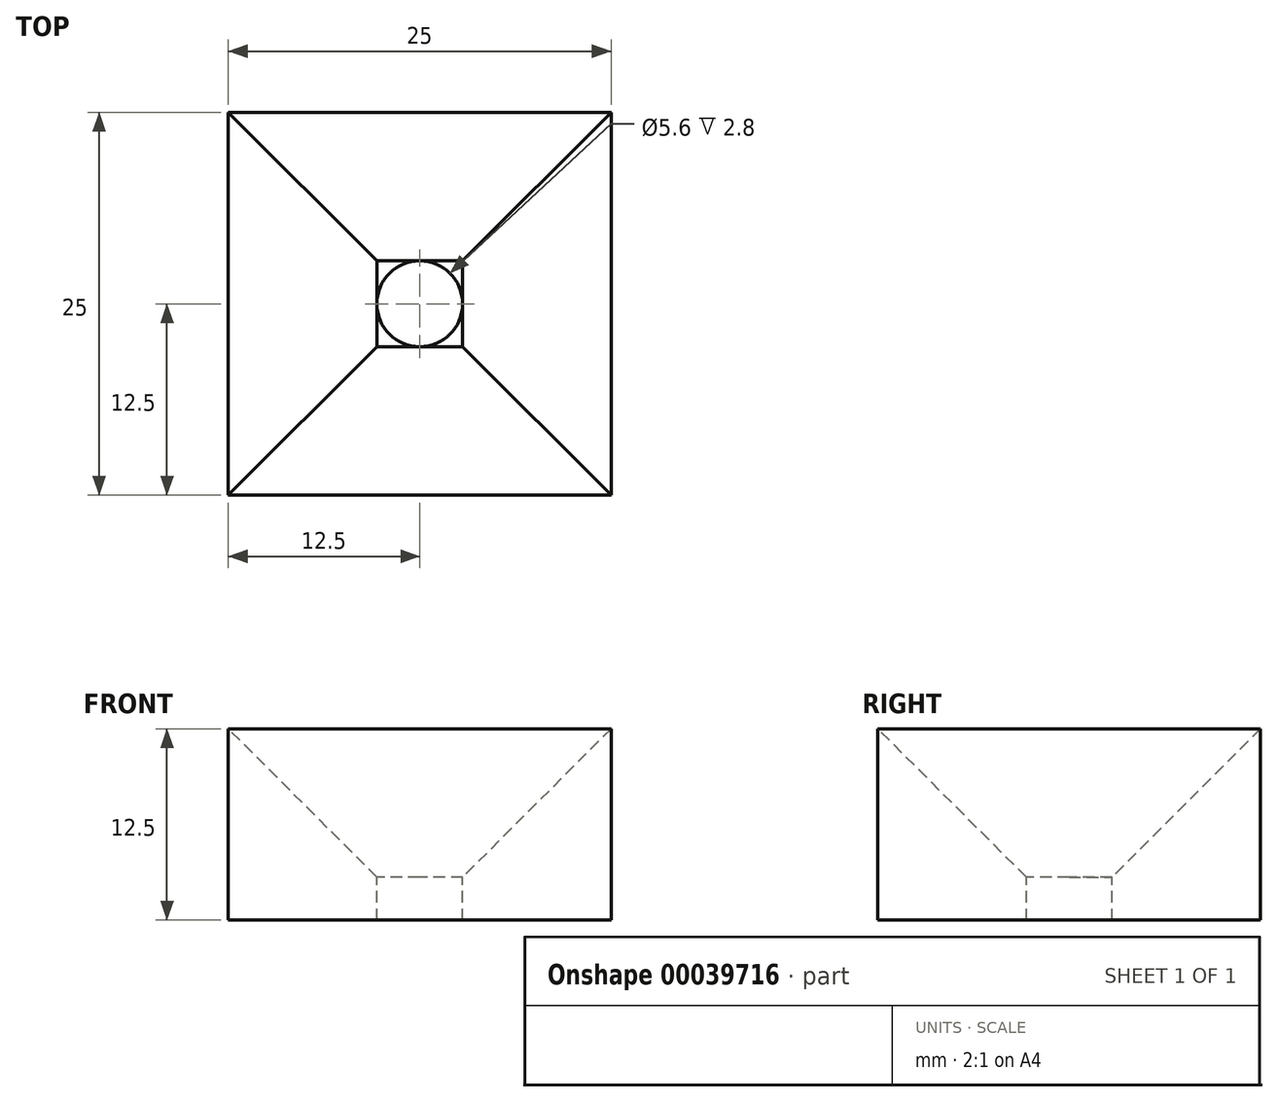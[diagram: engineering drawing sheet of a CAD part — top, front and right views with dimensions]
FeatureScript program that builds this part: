
annotation { "Feature Type Name" : "Feature", "Feature Type Description" : "" }
export const myFeature = defineFeature(function(context is Context, id is Id, definition is map)
    precondition{}
    {
        {
            var Q0;
            Q0=qCreatedBy(makeId("Front.planeOp"),FACE);
            var sketch = newSketch(context, id + "F0", { "sketchPlane" : qUnion([Q0])});
            skLineSegment(sketch, "E0.bottom", {"start": v(-12.5, 0) * mm, "end": v(12.5, 0) * mm});
            skLineSegment(sketch, "E0.top", {"start": v(-12.5, 12.5) * mm, "end": v(12.5, 12.5) * mm, "construction": true});
            skLineSegment(sketch, "E0.left", {"start": v(-12.5, 0) * mm, "end": v(-12.5, 12.5) * mm});
            skLineSegment(sketch, "E0.right", {"start": v(12.5, 0) * mm, "end": v(12.5, 12.5) * mm});
            skLineSegment(sketch, "E1", {"start": v(-12.5, 12.5) * mm, "end": v(0, 0) * mm});
            skLineSegment(sketch, "E2", {"start": v(0, 0) * mm, "end": v(12.5, 12.5) * mm});
            skLineSegment(sketch, "E3", {"start": v(-2.8, 2.8) * mm, "end": v(2.8, 2.8) * mm});
            skSolve(sketch);
        }
        {
            var Q0;
            Q0 = qSketchRegion(id + "F0", true);
            extrude(context, id + "F1", {"entities" : qUnion([Q0]), "oppositeDirection" : true, "depth" : 25 * mm});
        }
        {
            var Q0;
            Q0=makeQuery(id+"F1.opExtrude","SWEPT_FACE",FACE,{"disambiguationData":[OSD([sQuery(id+"F0.wireOp",EDGE,"E0.right")])]});
            var sketch = newSketch(context, id + "F2", { "sketchPlane" : qUnion([Q0])});
            skLineSegment(sketch, "E4", {"start": v(12.5, 0) * mm, "end": v(0, 12.5) * mm});
            skLineSegment(sketch, "E5", {"start": v(0, 12.5) * mm, "end": v(0, 0) * mm});
            skLineSegment(sketch, "E6", {"start": v(0, 0) * mm, "end": v(12.5, 0) * mm});
            skLineSegment(sketch, "E7", {"start": v(25, 12.5) * mm, "end": v(12.5, 0) * mm});
            skLineSegment(sketch, "E8", {"start": v(25, 0) * mm, "end": v(25, 12.5) * mm});
            skLineSegment(sketch, "E9", {"start": v(12.5, 0) * mm, "end": v(25, 0) * mm});
            skSolve(sketch);
        }
        {
            var Q0;
            Q0 = qSketchRegion(id + "F2", true);
            extrude(context, id + "F3", {"entities" : qUnion([Q0]), "operationType" : NewBodyOperationType.ADD, "oppositeDirection" : true, "depth" : 25 * mm});
        }
        {
            var Q0;
            Q0=makeQuery(id+"F1.opExtrude","SWEPT_FACE",FACE,{"disambiguationData":[OSD([sQuery(id+"F0.wireOp",EDGE,"E3")])]});
            var sketch = newSketch(context, id + "F4", { "sketchPlane" : qUnion([Q0])});
            skCircle(sketch, "E10", {"center": v(0, 12.5) * mm, "radius": 2.8 * mm});
            skPoint(sketch, "E10.centerSnap0", {"position": v(-2.8, 12.5) * mm});
            skSolve(sketch);
        }
        {
            var Q0;
            Q0 = qSketchRegion(id + "F4", true);
            extrude(context, id + "F5", {"entities" : qUnion([Q0]), "operationType" : NewBodyOperationType.REMOVE, "endBound" : BoundingType.THROUGH_ALL, "oppositeDirection" : true, "depth" : 25 * mm});
        }
    });
